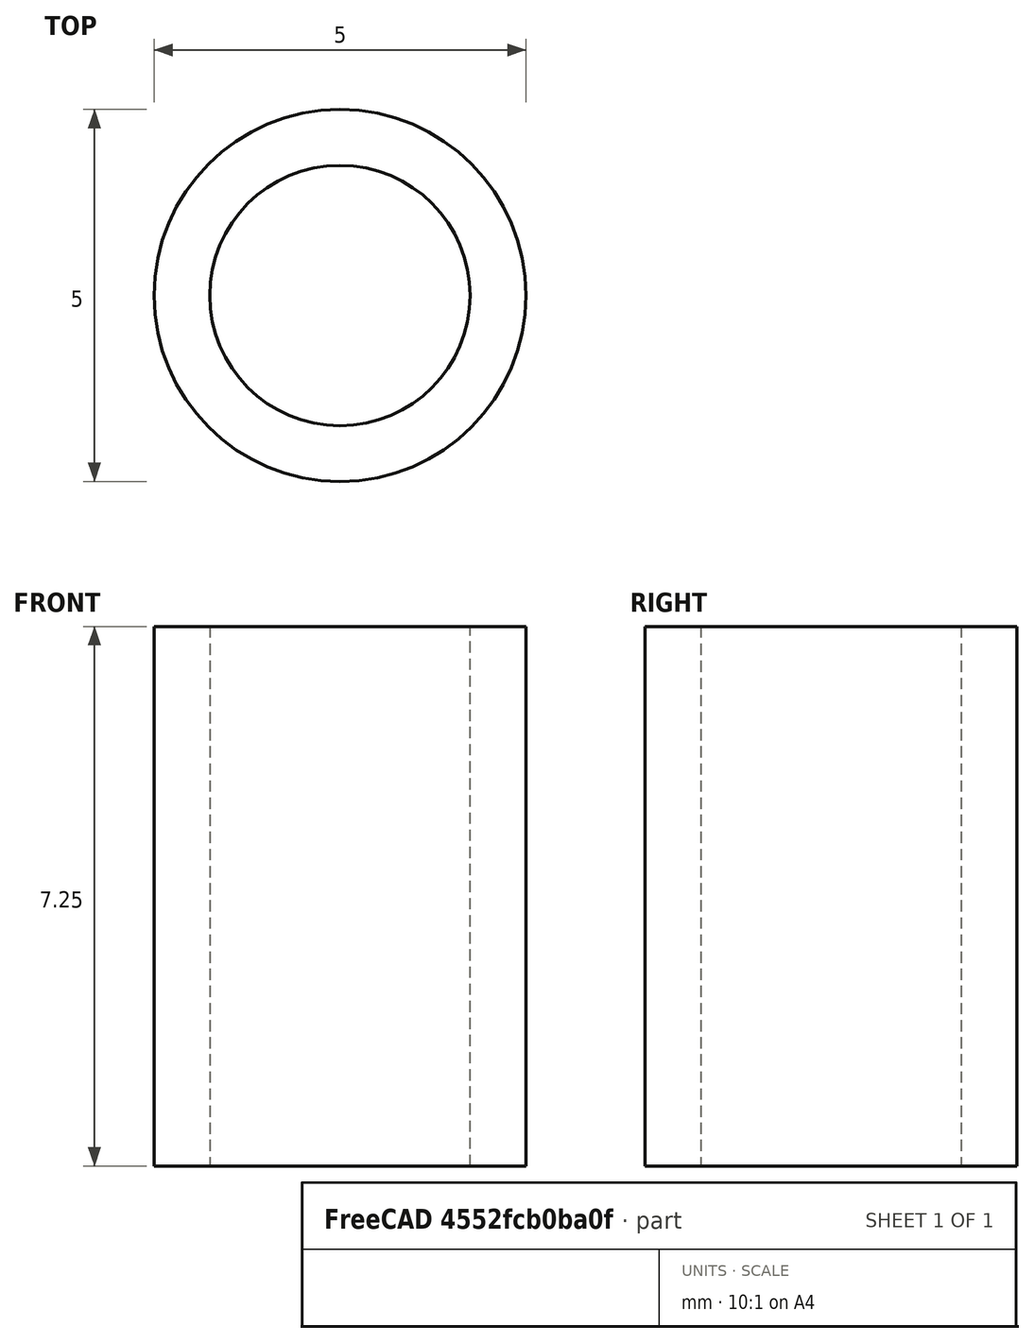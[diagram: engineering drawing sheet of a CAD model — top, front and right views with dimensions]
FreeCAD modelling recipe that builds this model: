
FCSTD DOCUMENT  (FreeCAD 0.20R29410 (Git))
Label: pcb-washer
License: All rights reserved
LicenseURL: http://en.wikipedia.org/wiki/All_rights_reserved
objects: Sketcher::SketchObject×1, PartDesign::Pad×1, PartDesign::Body×1
note: 4 computed .brp shape members not serialized (recipe doc carries the construction recipe); baked Part::Feature solids carry a one-line shape summary decoded from their .brp

FEATURE [Sketcher::SketchObject] Sketch
  FullyConstrained = true
  MapMode = 5
  Support = -> [XY_Plane]
  sketch-geometry (2):
    g0: Circle CenterX=0 CenterY=0 CenterZ=0 NormalX=0 NormalY=0 NormalZ=1 AngleXU=0 Radius=1.75
    g1: Circle CenterX=0 CenterY=0 CenterZ=0 NormalX=0 NormalY=0 NormalZ=1 AngleXU=0 Radius=2.5
  constraints (4):
    c: Coincident(g0,g-1)
    c: Coincident(g1,g0)
    c: Diameter(g0) = 3.5
    c: Diameter(g1) = 5
FEATURE [PartDesign::Pad] Pad
  Direction = (0,0,1)
  Length = 7.25
  Length2 = 10
  Profile = -> Sketch
  ReferenceAxis = -> Sketch [N_Axis]
  Type = 0
FEATURE [PartDesign::Body] Body
  Group = -> [Sketch,Pad]
  Origin = -> Origin
  Tip = -> Pad
